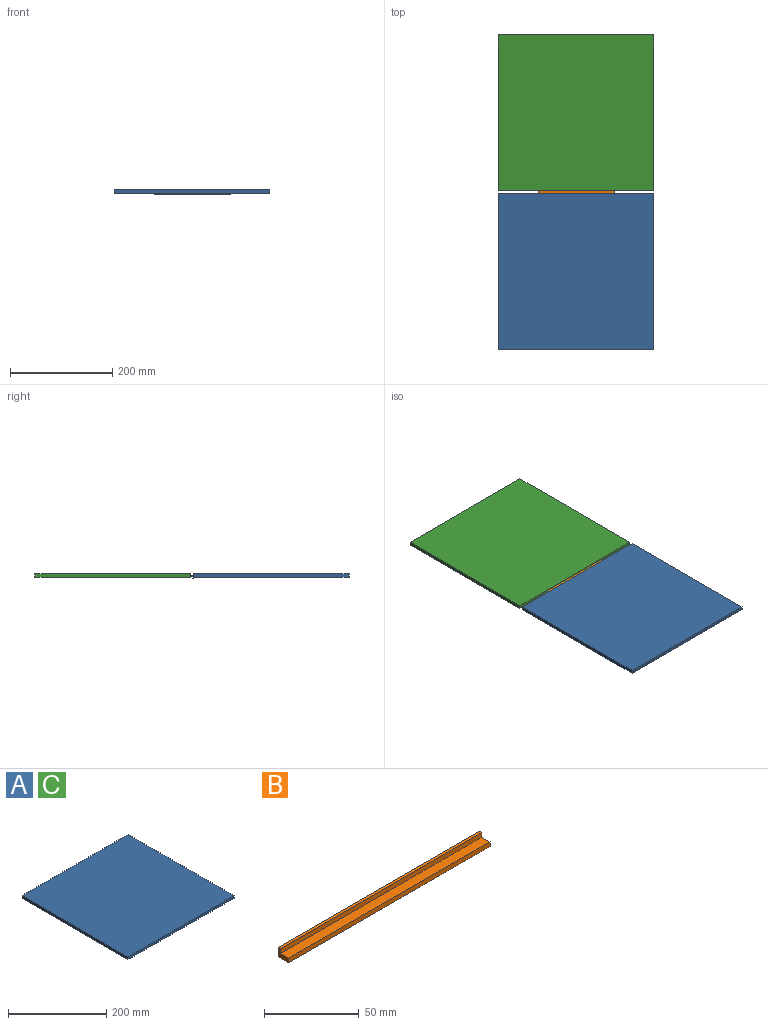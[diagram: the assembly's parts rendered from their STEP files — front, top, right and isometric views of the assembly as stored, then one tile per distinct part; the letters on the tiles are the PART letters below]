
ASSEMBLY  parts=3 mates=3
PART A: 6 faces, bbox 304.8x304.8x6.7 mm
  f0: plane 304.8x6.7mm, normal (-1,0,0), area 2042.2mm2, adj f1,f3,f4,f5
  f1: plane 304.8x6.7mm, normal (0,-1,0), area 2042.2mm2, adj f0,f2,f4,f5
  f2: plane 304.8x6.7mm, normal (1,0,0), area 2042.2mm2, adj f1,f3,f4,f5
  f3: plane 304.8x6.7mm, normal (0,1,0), area 2042.2mm2, adj f0,f2,f4,f5
  f4: plane 304.8x304.8mm, normal (0,0,1), area 92903mm2, adj f0,f1,f2,f3
  f5: plane 304.8x304.8mm, normal (0,0,-1), area 92903mm2, adj f0,f1,f2,f3
PART B: 8 faces, bbox 150x8x6 mm
  f0: plane 150x8mm, normal (0,0,-1), area 1200mm2, adj f1,f5,f6,f7
  f1: plane 150x6mm, normal (0,1,0), area 900mm2, adj f0,f2,f6,f7
  f2: plane 150x2mm, normal (0,0,1), area 300mm2, adj f1,f3,f6,f7
  f3: plane 150x3mm, normal (0,-1,0), area 450mm2, adj f2,f4,f6,f7
  f4: plane 150x6mm, normal (0,0,1), area 900mm2, adj f3,f5,f6,f7
  f5: plane 150x3mm, normal (0,-1,0), area 450mm2, adj f0,f4,f6,f7
  f6: plane 8x6mm, normal (1,0,0), area 30mm2, adj f0,f1,f2,f3,f4,f5
  f7: plane 8x6mm, normal (-1,0,0), area 30mm2, adj f0,f1,f2,f3,f4,f5
PART C: same geometry as A
PLACE A rot(axis=(0,-1,0),180deg) t=(2175.27,222.92,-1063.51)mm
PLACE B rot(axis=(1,0,0),180deg) t=(2003.51,472.77,-1066.42)mm
PLACE C rot(axis=(0,1,0),180deg) t=(2175.27,533.72,-1063.51)mm
MATE planar A.f3 <-> B.f1  axis (0,1,0) through (2077.82,472.77,-1066.86)mm
MATE parallel C.f4 <-> B.f2  axis (0,0,-1) through (2077.82,631.17,-1070.21)mm
MATE planar A.f4 <-> C.f4  axis (0,0,-1) through (2077.82,320.37,-1070.21)mm
